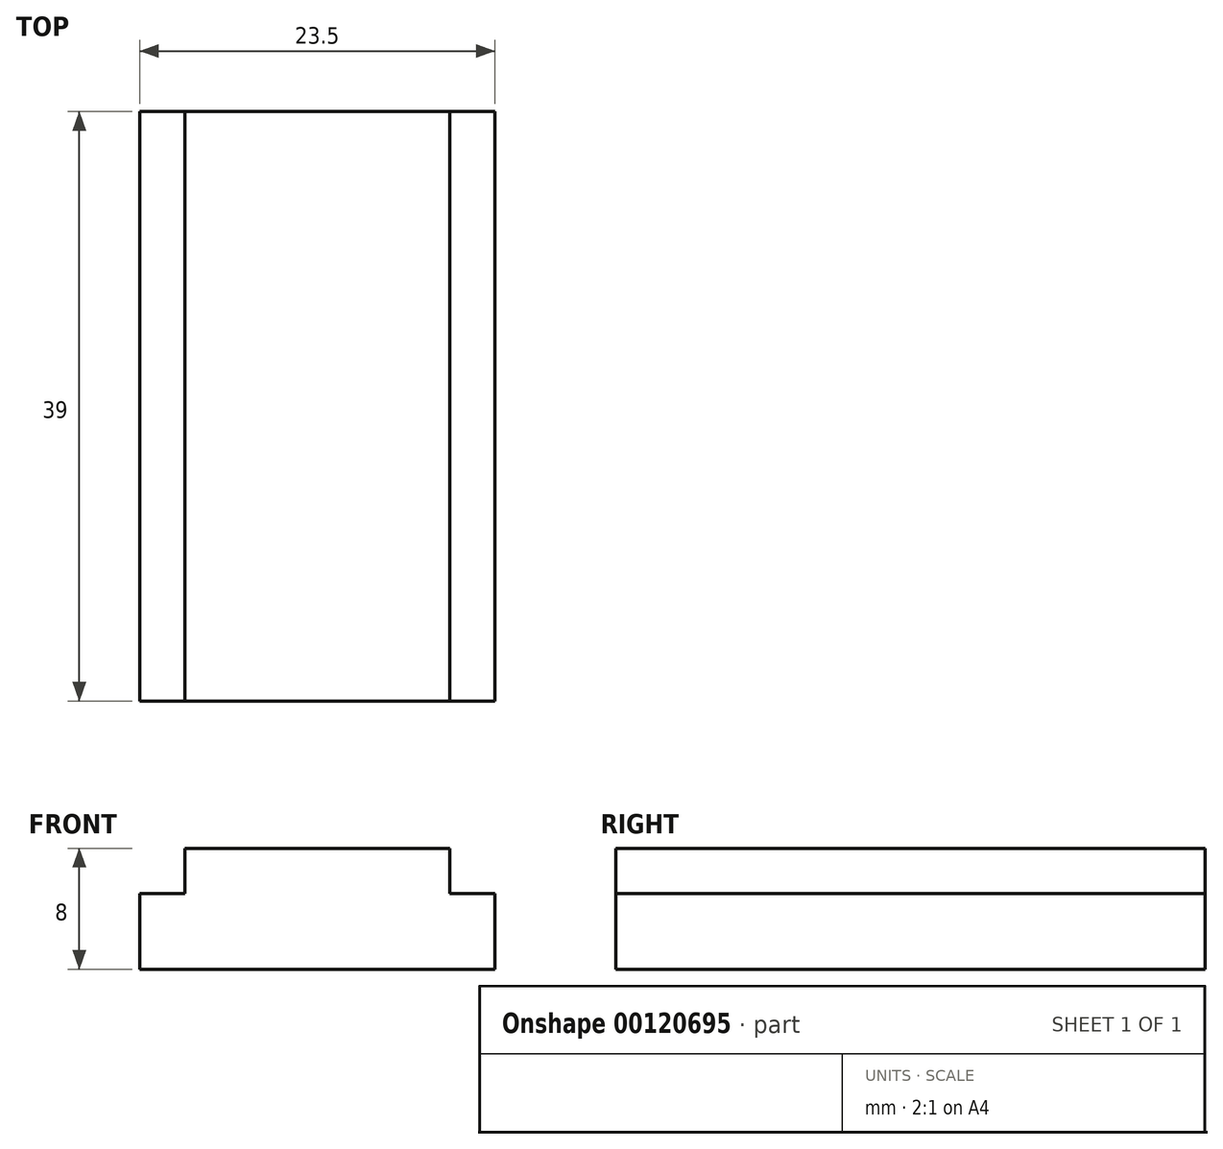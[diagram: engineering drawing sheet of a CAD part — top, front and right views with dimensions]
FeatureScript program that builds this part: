
annotation { "Feature Type Name" : "Feature", "Feature Type Description" : "" }
export const myFeature = defineFeature(function(context is Context, id is Id, definition is map)
    precondition{}
    {
        {
            var Q0;
            Q0=qCreatedBy(makeId("Front.planeOp"),FACE);
            var sketch = newSketch(context, id + "F0", { "sketchPlane" : qUnion([Q0])});
            skLineSegment(sketch, "E0", {"start": v(0, 0) * mm, "end": v(23.5, 0) * mm});
            skLineSegment(sketch, "E1", {"start": v(23.5, 0) * mm, "end": v(23.5, 5) * mm});
            skLineSegment(sketch, "E2", {"start": v(23.5, 5) * mm, "end": v(20.5, 5) * mm});
            skLineSegment(sketch, "E3", {"start": v(20.5, 5) * mm, "end": v(20.5, 8) * mm});
            skLineSegment(sketch, "E4", {"start": v(20.5, 8) * mm, "end": v(3, 8) * mm});
            skLineSegment(sketch, "E5", {"start": v(3, 8) * mm, "end": v(3, 5) * mm});
            skLineSegment(sketch, "E6", {"start": v(3, 5) * mm, "end": v(0, 5) * mm});
            skLineSegment(sketch, "E7", {"start": v(0, 5) * mm, "end": v(0, 0) * mm});
            skSolve(sketch);
        }
        {
            var Q0;
            Q0 = qSketchRegion(id + "F0", true);
            extrude(context, id + "F1", {"entities" : qUnion([Q0]), "depth" : 39 * mm});
        }
    });
